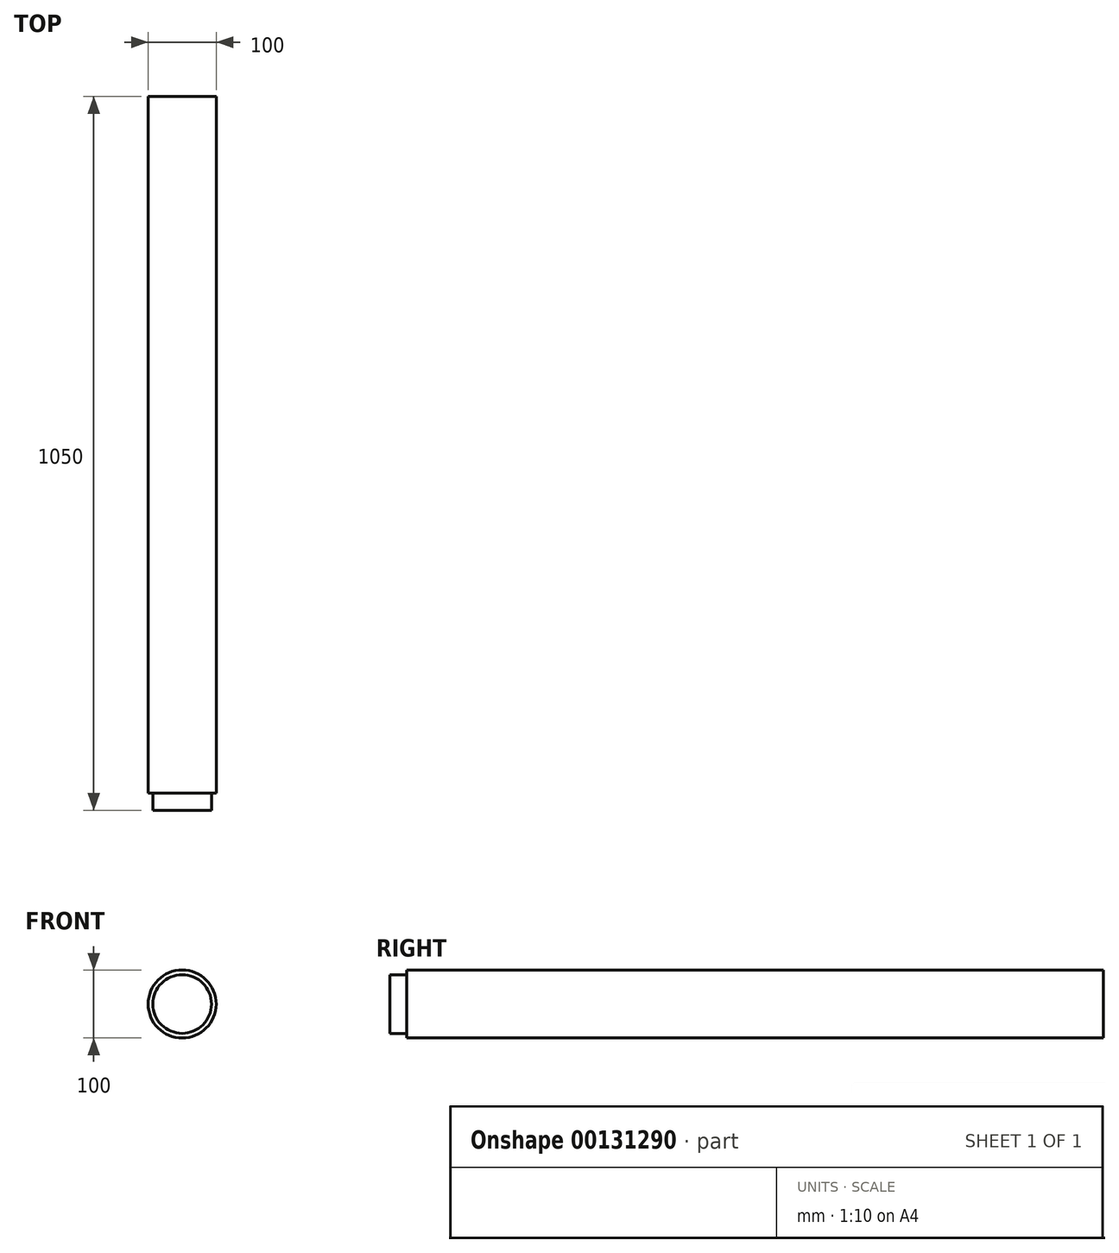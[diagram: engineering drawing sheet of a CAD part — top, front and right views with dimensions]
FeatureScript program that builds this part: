
annotation { "Feature Type Name" : "Feature", "Feature Type Description" : "" }
export const myFeature = defineFeature(function(context is Context, id is Id, definition is map)
    precondition{}
    {
        {
            var Q0;
            Q0=qCreatedBy(makeId("Front.planeOp"),FACE);
            var sketch = newSketch(context, id + "F0", { "sketchPlane" : qUnion([Q0])});
            skCircle(sketch, "E0", {"center": v(0, 0) * mm, "radius": 50 * mm});
            skSolve(sketch);
        }
        {
            var Q0;
            Q0=qSketchRegion(id+"F0",true);
            extrude(context, id + "F1", {"entities" : qUnion([Q0]), "endBound" : BoundingType.SYMMETRIC, "depth" : 1000 * mm});
        }
        {
            var Q0;
            Q0=qCreatedBy(makeId("Front.planeOp"),FACE);
            var sketch = newSketch(context, id + "F2", { "sketchPlane" : qUnion([Q0])});
            skCircle(sketch, "E1", {"center": v(0, 0) * mm, "radius": 44.43 * mm});
            skSolve(sketch);
        }
        {
            var Q0;
            Q0 = qSketchRegion(id + "F2", true);
            var Q1;
            Q1=makeQuery(id+"F1.opExtrude","CAP_FACE",FACE,{"disambiguationData":[OSD([sQuery(id+"F0.wireOp",EDGE,"E0")])],"isStart":false});
            extrude(context, id + "F3", {"entities" : qUnion([Q0, Q1]), "operationType" : NewBodyOperationType.ADD, "depth" : 25 * mm});
        }
        {
            var Q0;
            Q0=makeQuery(id+"F3.opExtrude","CAP_FACE",FACE,{"disambiguationData":[OSD([sQuery(id+"F0.wireOp",EDGE,"E0")])],"isStart":false});
            var sketch = newSketch(context, id + "F4", { "sketchPlane" : qUnion([Q0])});
            skCircle(sketch, "E2", {"center": v(0, 0) * mm, "radius": 43.1 * mm});
            skSolve(sketch);
        }
        {
            var Q0;
            Q0 = qSketchRegion(id + "F4", true);
            extrude(context, id + "F5", {"entities" : qUnion([Q0]), "operationType" : NewBodyOperationType.ADD, "depth" : 25 * mm});
        }
    });
